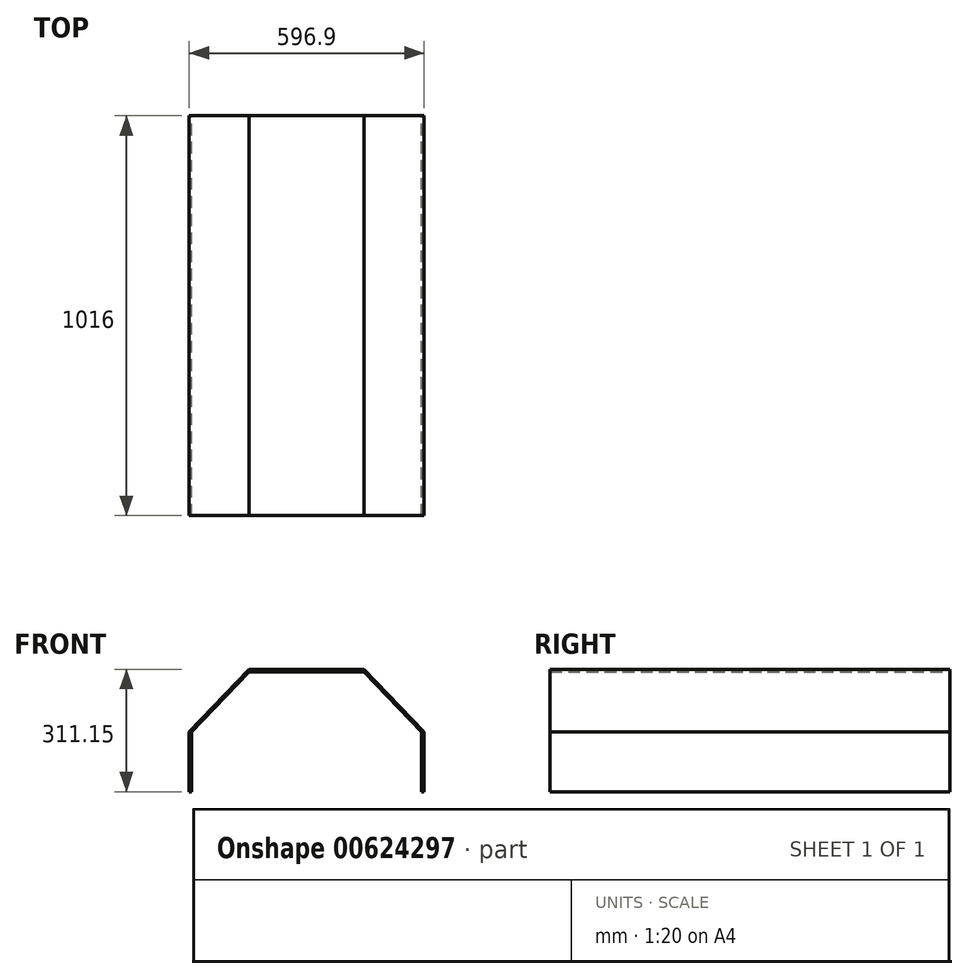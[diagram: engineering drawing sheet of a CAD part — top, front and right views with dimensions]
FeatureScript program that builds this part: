
annotation { "Feature Type Name" : "Feature", "Feature Type Description" : "" }
export const myFeature = defineFeature(function(context is Context, id is Id, definition is map)
    precondition{}
    {
        {
            var Q0;
            Q0=qCreatedBy(makeId("Front.planeOp"),FACE);
            var sketch = newSketch(context, id + "F0", { "sketchPlane" : qUnion([Q0])});
            skLineSegment(sketch, "E0", {"start": v(0, 0) * mm, "end": v(-254, 0) * mm});
            skLineSegment(sketch, "E1", {"start": v(0, 0) * mm, "end": v(254, 0) * mm});
            skSolve(sketch);
        }
        {
            var Q0;
            Q0=qCreatedBy(makeId("Front.planeOp"),FACE);
            var sketch = newSketch(context, id + "F1", { "sketchPlane" : qUnion([Q0])});
            skPoint(sketch, "E2.start.orphan", {"position": v(-127, 0) * mm});
            skPoint(sketch, "E3.end.orphan", {"position": v(127, 0) * mm});
            skLineSegment(sketch, "E4", {"start": v(-330.2, 253.09) * mm, "end": v(-330.2, 405.49) * mm});
            skLineSegment(sketch, "E5", {"start": v(254, 405.49) * mm, "end": v(254, 253.09) * mm});
            skPoint(sketch, "E6.endSnap0", {"position": v(254, 202.74) * mm});
            skPoint(sketch, "E7.start.orphan", {"position": v(-254, 0) * mm});
            skPoint(sketch, "E8.orphan", {"position": v(254, 0) * mm});
            skPoint(sketch, "E9.end.orphan", {"position": v(-127, 557.89) * mm});
            skPoint(sketch, "E10.end.orphan", {"position": v(127, 558.8) * mm});
            skPoint(sketch, "E11.start.orphan", {"position": v(127, 322.45) * mm});
            skPoint(sketch, "E12.end.orphan", {"position": v(-127, 322.45) * mm});
            skPoint(sketch, "E12.start.orphan", {"position": v(-127, 253.09) * mm});
            skPoint(sketch, "E13.end.orphan", {"position": v(-336.55, 405.49) * mm});
            skPoint(sketch, "E14.end.orphan", {"position": v(127, 488.04) * mm});
            skPoint(sketch, "E15.end.orphan", {"position": v(260.35, 405.49) * mm});
            skPoint(sketch, "E16.start.orphan", {"position": v(127, 481.69) * mm});
            skPoint(sketch, "E17.start.orphan", {"position": v(-127, 481.69) * mm});
            skLineSegment(sketch, "E18", {"start": v(107.95, 557.89) * mm, "end": v(-184.15, 557.89) * mm});
            skLineSegment(sketch, "E19", {"start": v(-184.15, 557.89) * mm, "end": v(-330.2, 405.49) * mm});
            skLineSegment(sketch, "E20", {"start": v(107.95, 557.89) * mm, "end": v(254, 405.49) * mm});
            skLineSegment(sketch, "E21", {"start": v(-330.2, 253.09) * mm, "end": v(-336.55, 253.09) * mm});
            skLineSegment(sketch, "E22", {"start": v(-336.55, 253.09) * mm, "end": v(-336.55, 405.49) * mm});
            skLineSegment(sketch, "E23", {"start": v(-184.15, 564.24) * mm, "end": v(107.95, 564.24) * mm});
            skLineSegment(sketch, "E24", {"start": v(-336.55, 405.49) * mm, "end": v(-184.15, 564.24) * mm});
            skLineSegment(sketch, "E25", {"start": v(254, 253.09) * mm, "end": v(260.35, 253.09) * mm});
            skLineSegment(sketch, "E26", {"start": v(260.35, 253.09) * mm, "end": v(260.35, 405.49) * mm});
            skLineSegment(sketch, "E27", {"start": v(260.35, 405.49) * mm, "end": v(107.95, 564.24) * mm});
            skPoint(sketch, "E28.start.orphan", {"position": v(-184.15, 253.09) * mm});
            skSolve(sketch);
        }
        {
            var Q0;
            Q0 = qSketchRegion(id + "F1", true);
            extrude(context, id + "F2", {"entities" : qUnion([Q0]), "depth" : 1016 * mm, "offsetDistance" : 25.4 * mm});
        }
    });
